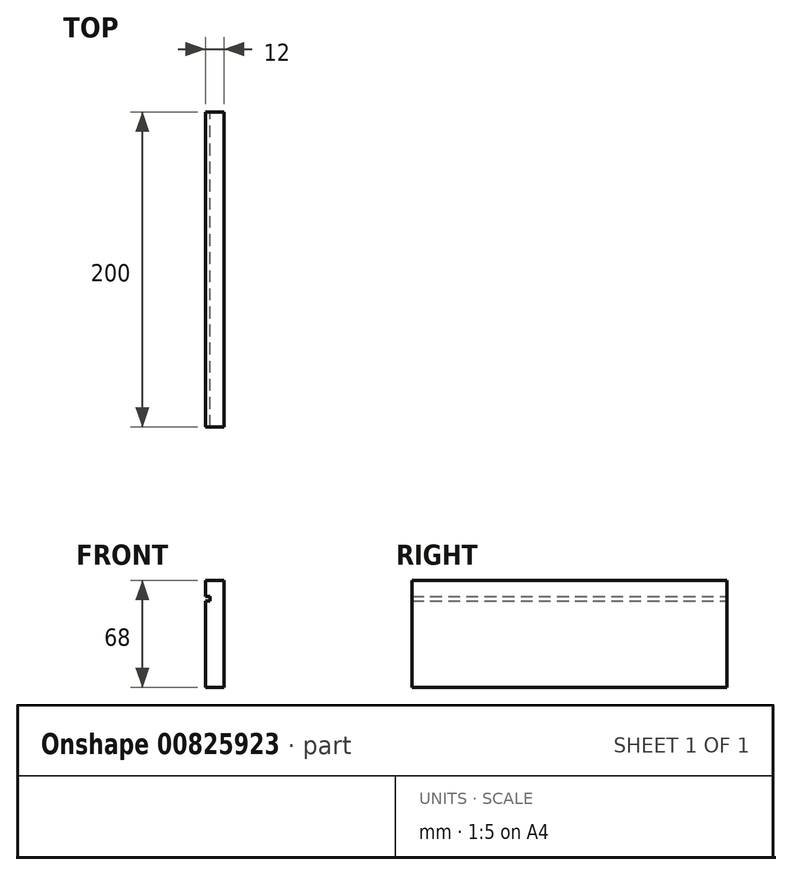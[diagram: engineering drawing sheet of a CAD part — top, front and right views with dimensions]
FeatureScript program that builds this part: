
annotation { "Feature Type Name" : "Feature", "Feature Type Description" : "" }
export const myFeature = defineFeature(function(context is Context, id is Id, definition is map)
    precondition{}
    {
        {
            var Q0;
            Q0=qCreatedBy(makeId("Front.planeOp"),FACE);
            var sketch = newSketch(context, id + "F0", { "sketchPlane" : qUnion([Q0])});
            skLineSegment(sketch, "E0.bottom", {"start": v(0, 68) * mm, "end": v(12, 68) * mm});
            skLineSegment(sketch, "E0.top", {"start": v(0, 0) * mm, "end": v(12, 0) * mm});
            skLineSegment(sketch, "E0.left", {"start": v(0, 68) * mm, "end": v(0, 58) * mm});
            skLineSegment(sketch, "E0.right", {"start": v(12, 68) * mm, "end": v(12, 0) * mm});
            skLineSegment(sketch, "E1.bottom", {"start": v(0, 58) * mm, "end": v(3, 58) * mm});
            skLineSegment(sketch, "E1.top", {"start": v(0, 55) * mm, "end": v(3, 55) * mm});
            skLineSegment(sketch, "E1.right", {"start": v(3, 58) * mm, "end": v(3, 55) * mm});
            skLineSegment(sketch, "E2.trimOffspring", {"start": v(0, 55) * mm, "end": v(0, 0) * mm});
            skSolve(sketch);
        }
        {
            var Q0;
            Q0 = qSketchRegion(id + "F0", true);
            extrude(context, id + "F1", {"entities" : qUnion([Q0]), "depth" : 200 * mm, "offsetDistance" : 25 * mm});
        }
    });
